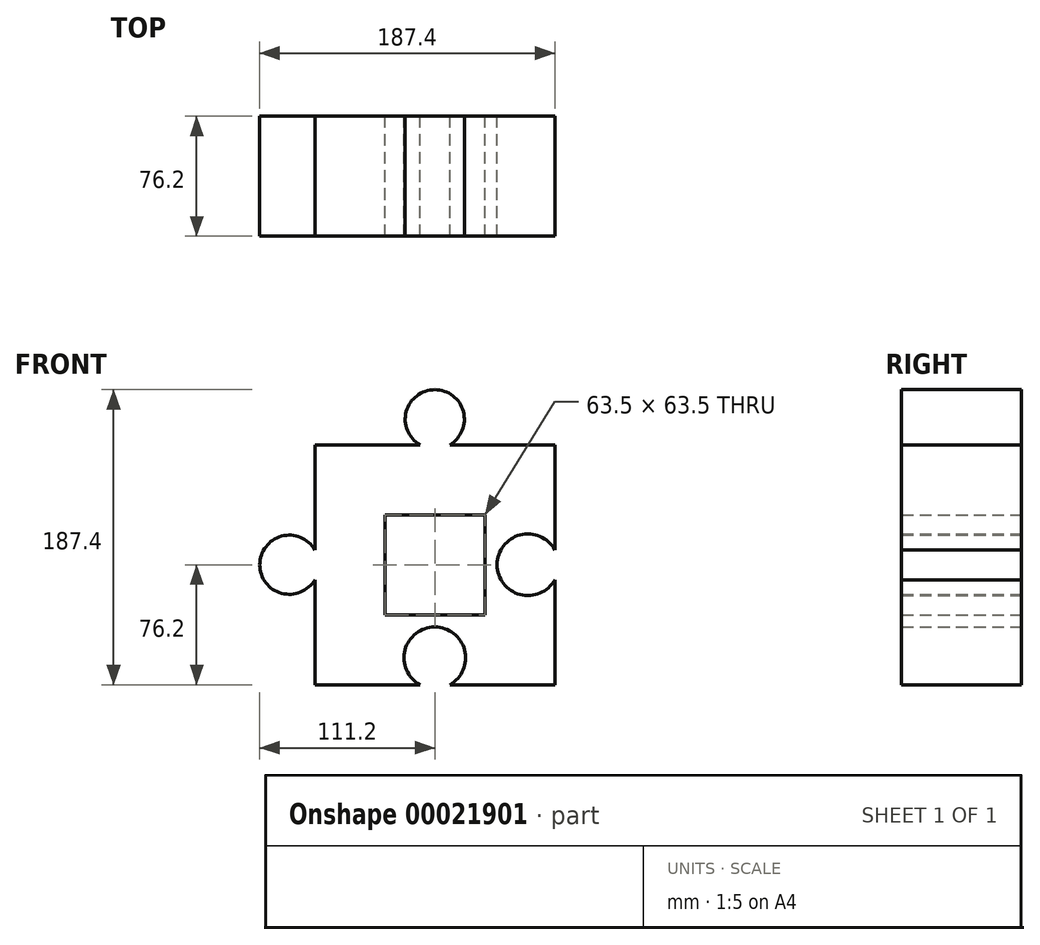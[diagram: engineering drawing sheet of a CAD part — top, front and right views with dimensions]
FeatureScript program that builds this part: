
annotation { "Feature Type Name" : "Feature", "Feature Type Description" : "" }
export const myFeature = defineFeature(function(context is Context, id is Id, definition is map)
    precondition{}
    {
        {
            var Q0;
            Q0=qCreatedBy(makeId("Front.planeOp"),FACE);
            var sketch = newSketch(context, id + "F0", { "sketchPlane" : qUnion([Q0])});
            skLineSegment(sketch, "E0.rect.bottom", {"start": v(-76.2, 76.2) * mm, "end": v(-9.53, 76.2) * mm});
            skLineSegment(sketch, "E0.rect.top", {"start": v(-76.2, -76.2) * mm, "end": v(-9.53, -76.2) * mm});
            skLineSegment(sketch, "E0.rect.left", {"start": v(-76.2, 76.2) * mm, "end": v(-76.2, 9.53) * mm});
            skLineSegment(sketch, "E0.rect.right", {"start": v(76.2, 76.2) * mm, "end": v(76.2, 9.52) * mm});
            skPoint(sketch, "E0.rect.middle", {"position": v(0, 0) * mm});
            skLineSegment(sketch, "E1.rect.bottom", {"start": v(31.75, 31.75) * mm, "end": v(-31.75, 31.75) * mm});
            skLineSegment(sketch, "E1.rect.top", {"start": v(31.75, -31.75) * mm, "end": v(-31.75, -31.75) * mm});
            skLineSegment(sketch, "E1.rect.left", {"start": v(31.75, 31.75) * mm, "end": v(31.75, -31.75) * mm});
            skLineSegment(sketch, "E1.rect.right", {"start": v(-31.75, 31.75) * mm, "end": v(-31.75, -31.75) * mm});
            skLineSegment(sketch, "E2.trimOffspring", {"start": v(-76.2, -9.52) * mm, "end": v(-76.2, -76.2) * mm});
            skPoint(sketch, "E3.center.orphan", {"position": v(-76.2, 0) * mm});
            skLineSegment(sketch, "E4.trimOffspring", {"start": v(76.2, -9.52) * mm, "end": v(76.2, -76.2) * mm});
            skPoint(sketch, "E5.center.orphan", {"position": v(76.2, 0) * mm});
            skLineSegment(sketch, "E6.trimOffspring", {"start": v(9.52, -76.2) * mm, "end": v(76.2, -76.2) * mm});
            skLineSegment(sketch, "E7.trimOffspring", {"start": v(9.52, 76.2) * mm, "end": v(76.2, 76.2) * mm});
            skPoint(sketch, "E8.center.orphan", {"position": v(0, -76.2) * mm});
            skArc(sketch, "E9", {"start": v(9.53, 76.2) * mm, "mid": v(0, 111.2) * mm, "end": v(-9.53, 76.2) * mm});
            skArc(sketch, "E10", {"start": v(-76.2, 9.53) * mm, "mid": v(-111.2, 0) * mm, "end": v(-76.2, -9.52) * mm});
            skArc(sketch, "E11", {"start": v(9.53, -76.2) * mm, "mid": v(0, -39.56) * mm, "end": v(-9.53, -76.2) * mm});
            skArc(sketch, "E12", {"start": v(76.2, 9.52) * mm, "mid": v(39.56, 0) * mm, "end": v(76.2, -9.52) * mm});
            skSolve(sketch);
        }
        {
            var Q0;
            Q0 = qSketchRegion(id + "F0", true);
            extrude(context, id + "F1", {"entities" : qUnion([Q0]), "depth" : 76.2 * mm});
        }
    });
